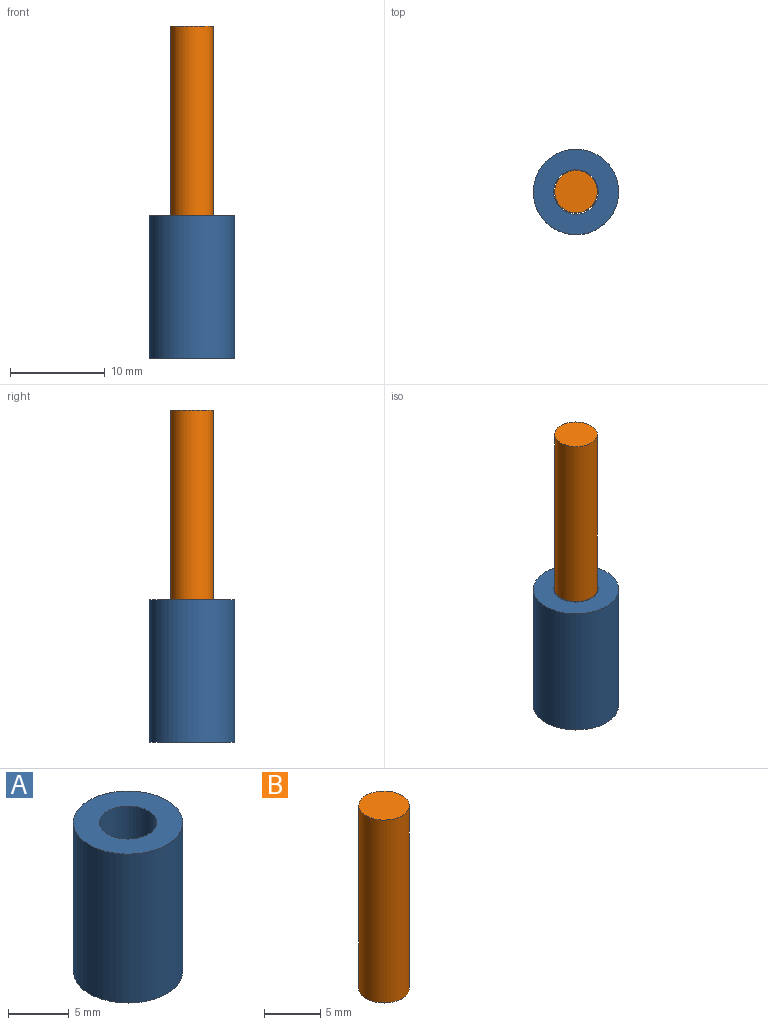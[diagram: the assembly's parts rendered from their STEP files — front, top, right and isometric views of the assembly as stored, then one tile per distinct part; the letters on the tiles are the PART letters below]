
ASSEMBLY  parts=2 mates=1
PART A: 4 faces, bbox 9x9x15 mm
  f0: cylinder r=2.35mm len=15mm, axis (0,0,-1), area 221.5mm2, adj f2,f3
  f1: cylinder r=4.5mm len=15mm, axis (0,0,-1), area 424.1mm2, adj f2,f3
  f2: plane 9x9mm, normal (0,0,1), area 46.3mm2, adj f0,f1
  f3: plane 9x9mm, normal (0,0,-1), area 46.3mm2, adj f0,f1
PART B: 3 faces, bbox 4.5x4.5x20 mm
  f0: cylinder r=2.25mm len=20mm, axis (0,0,-1), area 282.7mm2, adj f1,f2
  f1: plane 4.5x4.5mm, normal (0,0,1), area 15.9mm2, adj f0
  f2: plane 4.5x4.5mm, normal (0,0,-1), area 15.9mm2, adj f0
PLACE A rot(axis=(0,0,-1),57.9deg) t=(-22.15,-5.15,-6.26)mm fixed
PLACE B rot(axis=(0,0,-1),3.2deg) t=(-22.15,-5.15,8.74)mm
MATE revolute B.f0 <-> A.f1  axis (0,0,-1) through (-22.15,-5.15,8.74)mm
